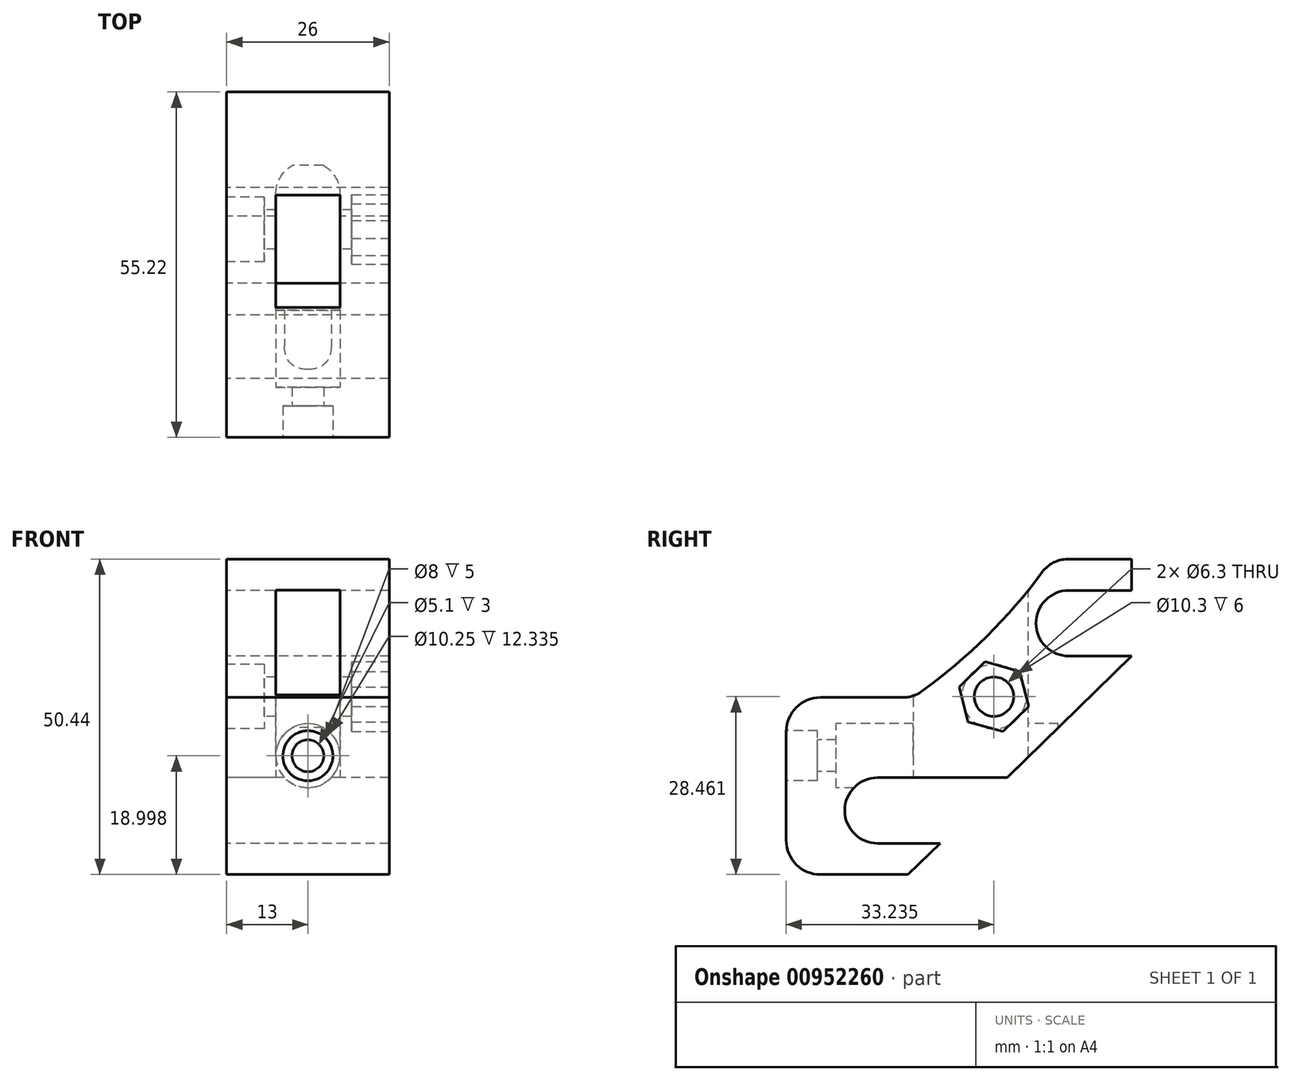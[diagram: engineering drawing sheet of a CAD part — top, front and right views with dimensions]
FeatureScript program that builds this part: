
annotation { "Feature Type Name" : "Feature", "Feature Type Description" : "" }
export const myFeature = defineFeature(function(context is Context, id is Id, definition is map)
    precondition{}
    {
        {
            var Q0;
            Q0=qCreatedBy(makeId("Right.planeOp"),FACE);
            var sketch = newSketch(context, id + "F0", { "sketchPlane" : qUnion([Q0])});
            skLineSegment(sketch, "E0", {"start": v(-22.1, 3.1) * mm, "end": v(-8.86, 3.1) * mm});
            skLineSegment(sketch, "E1", {"start": v(17.6, 9.72) * mm, "end": v(27.6, 9.72) * mm});
            skLineSegment(sketch, "E2", {"start": v(-12.98, -20.22) * mm, "end": v(-2.98, -20.22) * mm});
            skLineSegment(sketch, "E3", {"start": v(17.6, 20.22) * mm, "end": v(27.6, 20.22) * mm});
            skLineSegment(sketch, "E4", {"start": v(-12.98, -9.72) * mm, "end": v(7.75, -9.72) * mm});
            skLineSegment(sketch, "E5", {"start": v(27.6, 9.72) * mm, "end": v(7.75, -9.72) * mm});
            skLineSegment(sketch, "E6", {"start": v(17.4, 25.22) * mm, "end": v(27.6, 25.22) * mm});
            skLineSegment(sketch, "E7", {"start": v(27.6, 20.22) * mm, "end": v(27.6, 25.22) * mm});
            skLineSegment(sketch, "E8", {"start": v(-27.6, -2.4) * mm, "end": v(-27.6, -19.72) * mm});
            skLineSegment(sketch, "E9", {"start": v(-22.1, -25.22) * mm, "end": v(-8.08, -25.22) * mm});
            skArc(sketch, "E10", {"start": v(-22.1, 3.1) * mm, "mid": v(-26, 1.5) * mm, "end": v(-27.6, -2.4) * mm});
            skArc(sketch, "E11", {"start": v(-27.6, -19.72) * mm, "mid": v(-26, -23.61) * mm, "end": v(-22.1, -25.22) * mm});
            skLineSegment(sketch, "E12", {"start": v(-2.98, -20.22) * mm, "end": v(-8.08, -25.22) * mm});
            skCircle(sketch, "E13", {"center": v(5.62, 3.24) * mm, "radius": 3.15 * mm});
            skArc(sketch, "E14", {"start": v(17.6, 20.22) * mm, "mid": v(12.36, 14.97) * mm, "end": v(17.6, 9.72) * mm});
            skArc(sketch, "E15", {"start": v(-12.98, -9.72) * mm, "mid": v(-18.23, -14.97) * mm, "end": v(-12.98, -20.22) * mm});
            skLineSegment(sketch, "E16", {"start": v(-27.6, -2.22) * mm, "end": v(-27.6, -2.22) * mm});
            skArc(sketch, "E17", {"start": v(-5.93, 4.05) * mm, "mid": v(4.46, 12.87) * mm, "end": v(13.37, 23.19) * mm});
            skPoint(sketch, "E18.visualSharp", {"position": v(-7.27, 3.1) * mm});
            skArc(sketch, "E18.filletArc", {"start": v(-8.86, 3.1) * mm, "mid": v(-7.32, 3.35) * mm, "end": v(-5.93, 4.05) * mm});
            skPoint(sketch, "E19.visualSharp", {"position": v(14.83, 25.22) * mm});
            skArc(sketch, "E19.filletArc", {"start": v(17.4, 25.22) * mm, "mid": v(15.14, 24.68) * mm, "end": v(13.37, 23.19) * mm});
            skSolve(sketch);
        }
        {
            var Q0;
            Q0=makeQuery(id+"F0.imprint","IMPRINT",FACE,{"disambiguationData":[TD([[makeQuery(id+"F0.imprint","IMPRINT",EDGE,{"derivedFrom":sQuery(id+"F0.wireOp",EDGE,"cf56f78c-ab5c-453d-83a4-bda53a269bd4")}),-1.0]])]});
            var Q1;
            {var subQ1=sQuery(id+"F0.wireOp",EDGE,"E0");Q1=makeQuery(id+"F0.imprint","IMPRINT",FACE,{"disambiguationData":[TD([[makeQuery(id+"F0.imprint","IMPRINT",EDGE,{"derivedFrom":subQ1}),-1.0]])]});}
            extrude(context, id + "F1", {"entities" : qUnion([Q0, Q1]), "endBound" : BoundingType.SYMMETRIC, "depth" : 26 * mm, "offsetDistance" : 25 * mm});
        }
        {
            var Q0;
            Q0=makeQuery(id+"F1.opExtrude","CAP_FACE",FACE,{"disambiguationData":[OSD([sQuery(id+"F0.wireOp",EDGE,"cf56f78c-ab5c-453d-83a4-bda53a269bd4"),sQuery(id+"F0.wireOp",EDGE,"E0"),sQuery(id+"F0.wireOp",EDGE,"80502c63-e612-4486-ac1a-25ea61955544"),sQuery(id+"F0.wireOp",EDGE,"E1"),sQuery(id+"F0.wireOp",EDGE,"E2"),sQuery(id+"F0.wireOp",EDGE,"E3"),sQuery(id+"F0.wireOp",EDGE,"E4"),sQuery(id+"F0.wireOp",EDGE,"E5"),sQuery(id+"F0.wireOp",EDGE,"E6"),sQuery(id+"F0.wireOp",EDGE,"ec3e4a65-6fe2-47ca-b369-0a9f8bc8be81"),sQuery(id+"F0.wireOp",EDGE,"E7"),sQuery(id+"F0.wireOp",EDGE,"E8"),sQuery(id+"F0.wireOp",EDGE,"E9"),sQuery(id+"F0.wireOp",EDGE,"E10"),sQuery(id+"F0.wireOp",EDGE,"E11"),sQuery(id+"F0.wireOp",EDGE,"E12"),sQuery(id+"F0.wireOp",EDGE,"E13"),sQuery(id+"F0.wireOp",EDGE,"E14"),sQuery(id+"F0.wireOp",EDGE,"E15")])],"isStart":false});
            var sketch = newSketch(context, id + "F2", { "sketchPlane" : qUnion([Q0])});
            skCircle(sketch, "E20.cCircle", {"center": v(5.62, 3.24) * mm, "radius": 5.77 * mm, "construction": true});
            skLineSegment(sketch, "E20.0", {"start": v(11.19, 1.69) * mm, "end": v(7.06, -2.35) * mm});
            skLineSegment(sketch, "E20.1", {"start": v(7.06, -2.35) * mm, "end": v(1.5, -0.8) * mm});
            skLineSegment(sketch, "E20.2", {"start": v(1.5, -0.8) * mm, "end": v(0.06, 4.8) * mm});
            skLineSegment(sketch, "E20.3", {"start": v(0.06, 4.8) * mm, "end": v(4.19, 8.83) * mm});
            skLineSegment(sketch, "E20.4", {"start": v(4.19, 8.83) * mm, "end": v(9.75, 7.28) * mm});
            skLineSegment(sketch, "E20.5", {"start": v(9.75, 7.28) * mm, "end": v(11.19, 1.69) * mm});
            skSolve(sketch);
        }
        {
            var Q0;
            Q0=makeQuery(id+"F2.imprint","IMPRINT",FACE,{"disambiguationData":[TD([[makeQuery(id+"F2.imprint","IMPRINT",EDGE,{"derivedFrom":sQuery(id+"F2.wireOp",EDGE,"E20.0")}),-1.0]])]});
            extrude(context, id + "F3", {"entities" : qUnion([Q0]), "operationType" : NewBodyOperationType.REMOVE, "oppositeDirection" : true, "depth" : 6 * mm, "offsetDistance" : 25 * mm});
        }
        {
            var Q0;
            Q0=makeQuery(id+"F1.opExtrude","CAP_FACE",FACE,{"disambiguationData":[OSD([sQuery(id+"F0.wireOp",EDGE,"cf56f78c-ab5c-453d-83a4-bda53a269bd4"),sQuery(id+"F0.wireOp",EDGE,"E0"),sQuery(id+"F0.wireOp",EDGE,"80502c63-e612-4486-ac1a-25ea61955544"),sQuery(id+"F0.wireOp",EDGE,"E1"),sQuery(id+"F0.wireOp",EDGE,"E2"),sQuery(id+"F0.wireOp",EDGE,"E3"),sQuery(id+"F0.wireOp",EDGE,"E4"),sQuery(id+"F0.wireOp",EDGE,"E5"),sQuery(id+"F0.wireOp",EDGE,"E6"),sQuery(id+"F0.wireOp",EDGE,"ec3e4a65-6fe2-47ca-b369-0a9f8bc8be81"),sQuery(id+"F0.wireOp",EDGE,"E7"),sQuery(id+"F0.wireOp",EDGE,"E8"),sQuery(id+"F0.wireOp",EDGE,"E9"),sQuery(id+"F0.wireOp",EDGE,"E10"),sQuery(id+"F0.wireOp",EDGE,"E11"),sQuery(id+"F0.wireOp",EDGE,"E12"),sQuery(id+"F0.wireOp",EDGE,"E13"),sQuery(id+"F0.wireOp",EDGE,"E14"),sQuery(id+"F0.wireOp",EDGE,"E15")])],"isStart":true});
            var sketch = newSketch(context, id + "F4", { "sketchPlane" : qUnion([Q0])});
            skCircle(sketch, "E21", {"center": v(-5.62, 3.24) * mm, "radius": 5.15 * mm});
            skSolve(sketch);
        }
        {
            var Q0;
            Q0=makeQuery(id+"F4.imprint","IMPRINT",FACE,{"disambiguationData":[TD([[makeQuery(id+"F4.imprint","IMPRINT",EDGE,{"derivedFrom":sQuery(id+"F4.wireOp",EDGE,"E21")}),1.0]])]});
            extrude(context, id + "F5", {"entities" : qUnion([Q0]), "operationType" : NewBodyOperationType.REMOVE, "oppositeDirection" : true, "depth" : 6 * mm, "offsetDistance" : 25 * mm});
        }
        {
            var Q0;
            Q0=qCreatedBy(makeId("Right.planeOp"),FACE);
            var sketch = newSketch(context, id + "F6", { "sketchPlane" : qUnion([Q0])});
            skLineSegment(sketch, "E22", {"start": v(11.12, -6.41) * mm, "end": v(11.12, 21.12) * mm});
            skLineSegment(sketch, "E23", {"start": v(-7.27, -9.72) * mm, "end": v(7.75, -9.72) * mm});
            skLineSegment(sketch, "E24", {"start": v(11.12, -6.41) * mm, "end": v(7.75, -9.72) * mm});
            skLineSegment(sketch, "E25", {"start": v(-7.27, 3.1) * mm, "end": v(-7.27, -9.72) * mm});
            skLineSegment(sketch, "E26", {"start": v(-7.27, 3.1) * mm, "end": v(11.12, 21.12) * mm});
            skSolve(sketch);
        }
        {
            var Q0;
            Q0 = qSketchRegion(id + "F6", true);
            extrude(context, id + "F7", {"entities" : qUnion([Q0]), "operationType" : NewBodyOperationType.REMOVE, "endBound" : BoundingType.SYMMETRIC, "depth" : 10.25 * mm, "offsetDistance" : 25 * mm});
        }
        {
            var Q0;
            Q0=qCreatedBy(makeId("Right.planeOp"),FACE);
            var sketch = newSketch(context, id + "F8", { "sketchPlane" : qUnion([Q0])});
            skLineSegment(sketch, "E27", {"start": v(-19.6, -1.1) * mm, "end": v(15.91, -1.1) * mm});
            skLineSegment(sketch, "E28", {"start": v(15.91, -6.22) * mm, "end": v(-27.6, -6.22) * mm});
            skLineSegment(sketch, "E29", {"start": v(-19.6, -3.67) * mm, "end": v(-22.6, -3.67) * mm});
            skLineSegment(sketch, "E30", {"start": v(-22.6, -2.22) * mm, "end": v(-27.6, -2.22) * mm});
            skLineSegment(sketch, "E31", {"start": v(-22.6, -2.22) * mm, "end": v(-22.6, -3.67) * mm});
            skLineSegment(sketch, "E32", {"start": v(-27.6, -6.22) * mm, "end": v(-27.6, -2.22) * mm});
            skLineSegment(sketch, "E33", {"start": v(15.91, -6.22) * mm, "end": v(15.91, -1.1) * mm});
            skLineSegment(sketch, "E34", {"start": v(-19.6, -1.1) * mm, "end": v(-19.6, -3.67) * mm});
            skSolve(sketch);
        }
        {
            var Q0;
            Q0 = qSketchRegion(id + "F8", true);
            var Q1;
            Q1=sQuery(id+"F8.wireOp",EDGE,"E28");
            revolve(context, id + "F9", {"operationType" : NewBodyOperationType.REMOVE, "surfaceOperationType" : NewSurfaceOperationType.NEW, "entities" : qUnion([Q0]), "axis" : qUnion([Q1]), "revolveType" : RevolveType.FULL, "oppositeDirection" : true});
        }
    });
